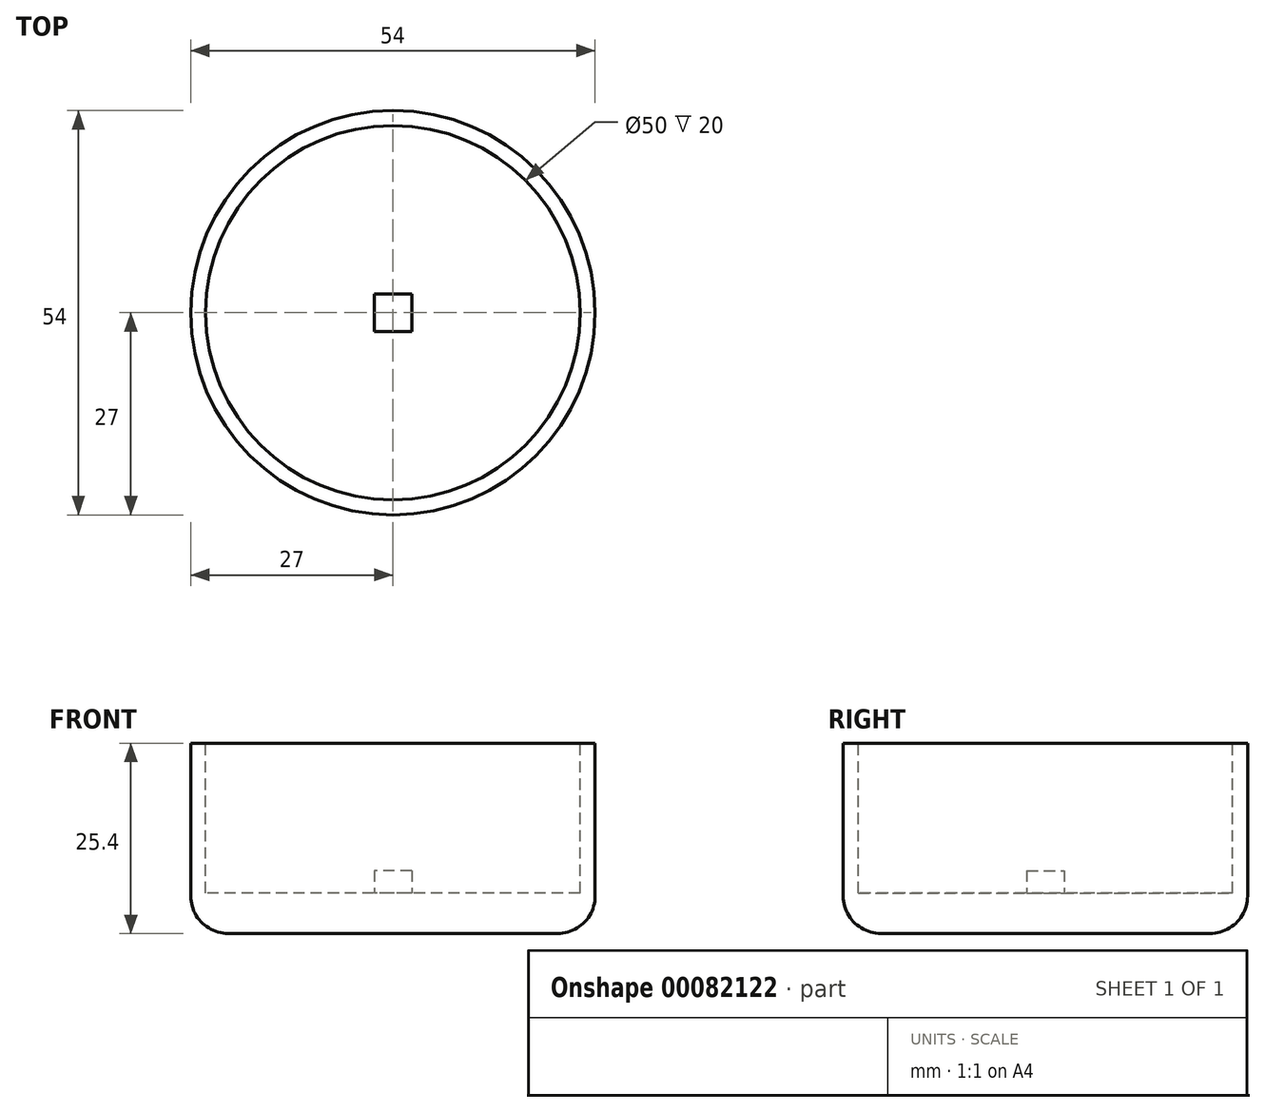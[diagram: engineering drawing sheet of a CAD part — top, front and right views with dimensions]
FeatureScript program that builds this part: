
annotation { "Feature Type Name" : "Feature", "Feature Type Description" : "" }
export const myFeature = defineFeature(function(context is Context, id is Id, definition is map)
    precondition{}
    {
        {
            var Q0;
            Q0=qCreatedBy(makeId("Top.planeOp"),FACE);
            var sketch = newSketch(context, id + "F0", { "sketchPlane" : qUnion([Q0])});
            skCircle(sketch, "E0", {"center": v(0, 0) * mm, "radius": 27 * mm});
            skSolve(sketch);
        }
        {
            var Q0;
            Q0=makeQuery(id+"F0.imprint","IMPRINT",FACE,{"disambiguationData":[TD([[makeQuery(id+"F0.imprint","IMPRINT",EDGE,{"derivedFrom":sQuery(id+"F0.wireOp",EDGE,"E0")}),1.0]])]});
            extrude(context, id + "F5", {"entities" : qUnion([Q0]), "depth" : 25.4 * mm});
        }
        {
            var Q0;
            Q0=makeQuery(id+"F5.opExtrude","CAP_FACE",FACE,{"disambiguationData":[OSD([sQuery(id+"F0.wireOp",EDGE,"E0")])],"isStart":false});
            var sketch = newSketch(context, id + "F1", { "sketchPlane" : qUnion([Q0])});
            skCircle(sketch, "E1", {"center": v(0, 0) * mm, "radius": 25 * mm});
            skSolve(sketch);
        }
        {
            var Q0;
            Q0=makeQuery(id+"F1.imprint","IMPRINT",FACE,{"disambiguationData":[TD([[makeQuery(id+"F1.imprint","IMPRINT",EDGE,{"derivedFrom":sQuery(id+"F1.wireOp",EDGE,"E1")}),1.0]])]});
            extrude(context, id + "F2", {"entities" : qUnion([Q0]), "operationType" : NewBodyOperationType.REMOVE, "oppositeDirection" : true, "depth" : 20 * mm});
        }
        {
            var Q0;
            Q0=makeQuery(id+"F5.opExtrude","CAP_EDGE",EDGE,{"disambiguationData":[OSD([sQuery(id+"F0.wireOp",EDGE,"E0")])],"isStart":true});
            fillet(context, id + "F3", {"entities" : qUnion([Q0]), "radius" : 5 * mm, "tangentPropagation" : true, "allowEdgeOverflow" : false});
        }
        {
            var Q0;
            Q0=makeQuery(id+"F2.boolean.opBoolean","COPY",FACE,{"derivedFrom":makeQuery(id+"F2.opExtrude","CAP_FACE",FACE,{"disambiguationData":[OSD([sQuery(id+"F1.wireOp",EDGE,"E1")])],"isStart":false})});
            var sketch = newSketch(context, id + "F4", { "sketchPlane" : qUnion([Q0])});
            skLineSegment(sketch, "E2.bottom", {"start": v(2.5, -2.5) * mm, "end": v(-2.5, -2.5) * mm});
            skLineSegment(sketch, "E2.top", {"start": v(2.5, 2.5) * mm, "end": v(-2.5, 2.5) * mm});
            skLineSegment(sketch, "E2.left", {"start": v(2.5, -2.5) * mm, "end": v(2.5, 2.5) * mm});
            skLineSegment(sketch, "E2.right", {"start": v(-2.5, -2.5) * mm, "end": v(-2.5, 2.5) * mm});
            skPoint(sketch, "E2.middle", {"position": v(0, 0) * mm});
            skSolve(sketch);
        }
        {
            var Q0;
            Q0=makeQuery(id+"F4.imprint","IMPRINT",FACE,{"disambiguationData":[TD([[makeQuery(id+"F4.imprint","IMPRINT",EDGE,{"derivedFrom":sQuery(id+"F4.wireOp",EDGE,"E2.bottom")}),-1.0]])]});
            extrude(context, id + "F6", {"entities" : qUnion([Q0]), "operationType" : NewBodyOperationType.ADD, "depth" : 3 * mm});
        }
    });
